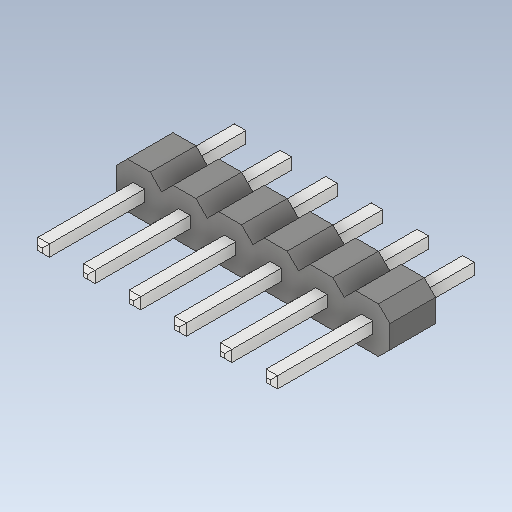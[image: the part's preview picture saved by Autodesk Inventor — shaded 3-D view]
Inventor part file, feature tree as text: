
AUTODESK INVENTOR PART (.ipt)
format: ipt  version: 2020 (Build 240168000, 168)  size: 192,512 bytes
history: imported  units: in
note: dims shown in document units (in); Inventor stores cm internally (conversion verified against a paired STEP export)
features: imported_body x1
ambient origin geometry x8: Origin, YZ Plane, XZ Plane, XY Plane, X Axis, Y Axis, Z Axis, Center Point
bodies: Solid1 (imported_parasolid), Body2 (imported_parasolid)
feature tree (1):
  imported_body  NMx_Import_Brep_tag  [imported B-rep: ~148 faces, bbox_mm=[15.24, 2.54, 11.34]]
